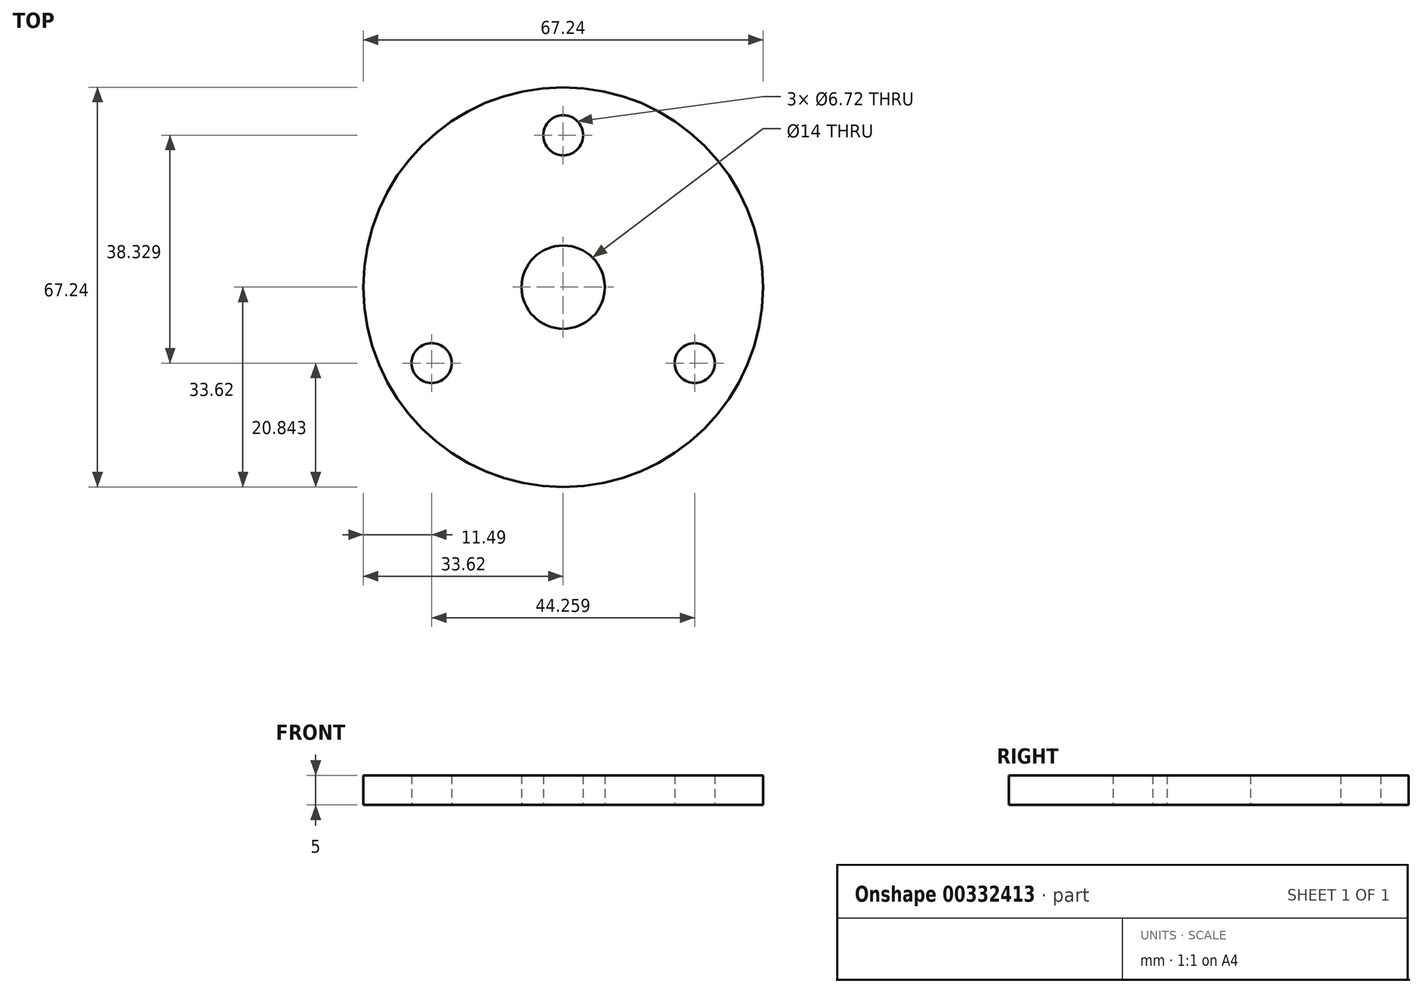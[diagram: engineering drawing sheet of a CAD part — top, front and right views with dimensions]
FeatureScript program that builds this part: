
annotation { "Feature Type Name" : "Feature", "Feature Type Description" : "" }
export const myFeature = defineFeature(function(context is Context, id is Id, definition is map)
    precondition{}
    {
        {
            var Q0;
            Q0=qCreatedBy(makeId("Top.planeOp"),FACE);
            var sketch = newSketch(context, id + "F0", { "sketchPlane" : qUnion([Q0])});
            skCircle(sketch, "E0", {"center": v(0, 0) * mm, "radius": 33.62 * mm});
            skCircle(sketch, "E1", {"center": v(0, 25.55) * mm, "radius": 3.36 * mm});
            skCircle(sketch, "E2", {"center": v(22.13, -12.78) * mm, "radius": 3.36 * mm});
            skCircle(sketch, "E3", {"center": v(-22.13, -12.78) * mm, "radius": 3.36 * mm});
            skCircle(sketch, "E4", {"center": v(0, 0) * mm, "radius": 7 * mm});
            skSolve(sketch);
        }
        {
            var Q0;
            Q0=makeQuery(id+"F0.imprint","IMPRINT",FACE,{"disambiguationData":[TD([[makeQuery(id+"F0.imprint","IMPRINT",EDGE,{"derivedFrom":sQuery(id+"F0.wireOp",EDGE,"E0")}),1.0]])]});
            extrude(context, id + "F1", {"entities" : qUnion([Q0]), "depth" : 5 * mm});
        }
    });
